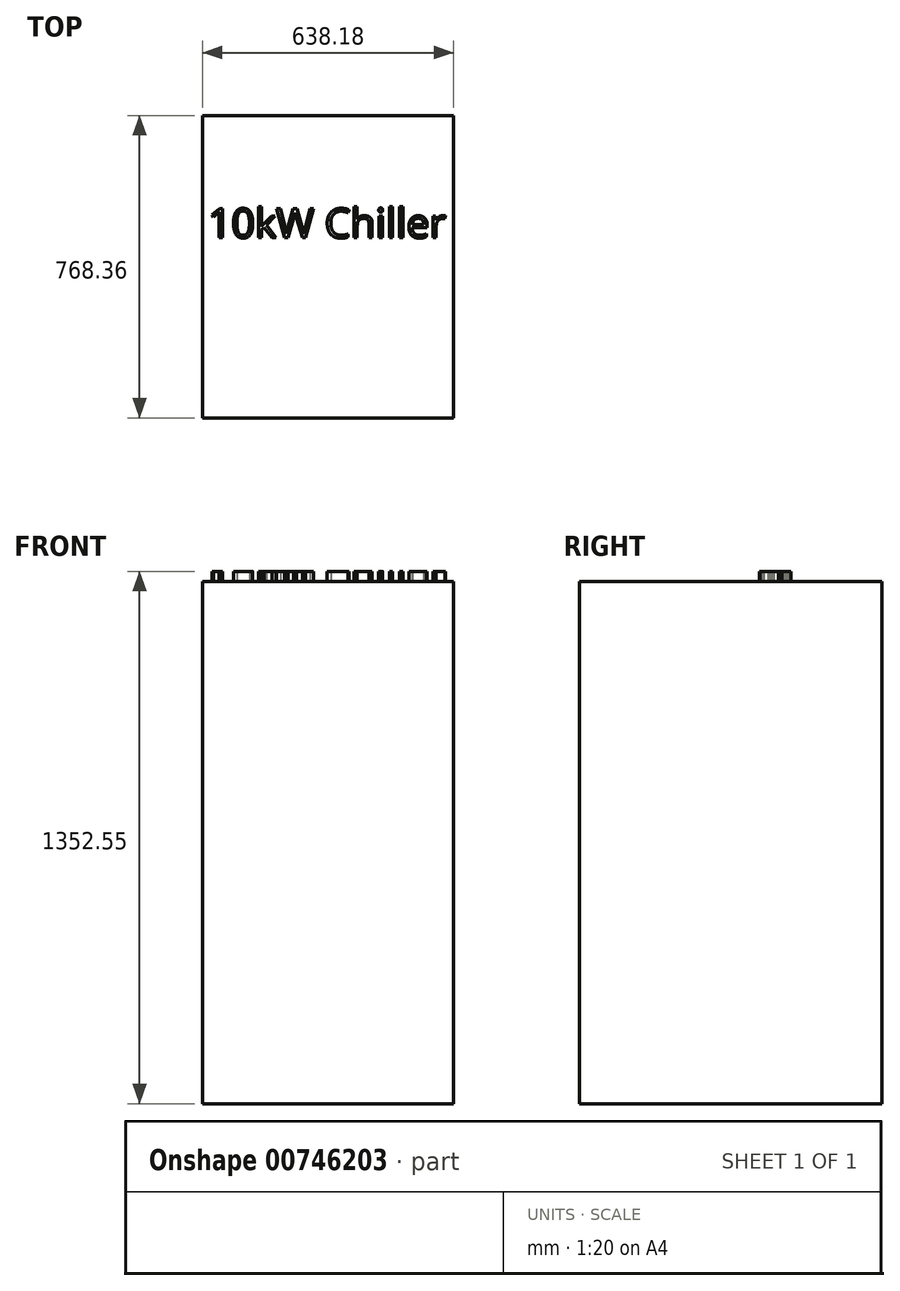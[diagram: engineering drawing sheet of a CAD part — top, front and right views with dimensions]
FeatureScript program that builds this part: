
annotation { "Feature Type Name" : "Feature", "Feature Type Description" : "" }
export const myFeature = defineFeature(function(context is Context, id is Id, definition is map)
    precondition{}
    {
        {
            var Q0;
            Q0=qCreatedBy(makeId("Top.planeOp"),FACE);
            var sketch = newSketch(context, id + "F0", { "sketchPlane" : qUnion([Q0])});
            skLineSegment(sketch, "E0.bottom", {"start": v(319.09, -384.18) * mm, "end": v(-319.09, -384.18) * mm});
            skLineSegment(sketch, "E0.top", {"start": v(319.09, 384.18) * mm, "end": v(-319.09, 384.18) * mm});
            skLineSegment(sketch, "E0.left", {"start": v(319.09, -384.18) * mm, "end": v(319.09, 384.18) * mm});
            skLineSegment(sketch, "E0.right", {"start": v(-319.09, -384.18) * mm, "end": v(-319.09, 384.18) * mm});
            skPoint(sketch, "E0.middle", {"position": v(0, 0) * mm});
            skSolve(sketch);
        }
        {
            var Q0;
            Q0=makeQuery(id+"F0.imprint","IMPRINT",FACE,{"disambiguationData":[TD([[makeQuery(id+"F0.imprint","IMPRINT",EDGE,{"derivedFrom":sQuery(id+"F0.wireOp",EDGE,"E0.bottom")}),-1.0]])]});
            extrude(context, id + "F1", {"entities" : qUnion([Q0]), "depth" : 1327.15 * mm, "offsetDistance" : 25.4 * mm});
        }
        {
            var Q0;
            Q0=makeQuery(id+"F1.opExtrude","CAP_FACE",FACE,{"disambiguationData":[OSD([sQuery(id+"F0.wireOp",EDGE,"E0.bottom"),sQuery(id+"F0.wireOp",EDGE,"E0.top"),sQuery(id+"F0.wireOp",EDGE,"E0.left"),sQuery(id+"F0.wireOp",EDGE,"E0.right")])],"isStart":false});
            var sketch = newSketch(context, id + "F2", { "sketchPlane" : qUnion([Q0])});
            skText(sketch, "E1", { "text": "10kW Chiller\n", "fontName": "OpenSans-Regular.ttf"});
            const initialGuessF2  = {"E1": [-0.3048, 0.07321, 1, 0, 0.07468]};
            skSetInitialGuess(sketch, initialGuessF2);
            skSolve(sketch);
        }
        {
            var Q0;
            Q0 = qSketchRegion(id + "F2", true);
            extrude(context, id + "F3", {"entities" : qUnion([Q0]), "operationType" : NewBodyOperationType.ADD, "depth" : 25.4 * mm, "offsetDistance" : 25.4 * mm});
        }
    });
